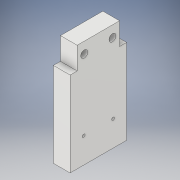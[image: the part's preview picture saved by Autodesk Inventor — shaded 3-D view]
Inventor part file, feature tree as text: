
AUTODESK INVENTOR PART (.ipt)
format: ipt  version: 2017 (Build 210142000, 142)  size: 136,192 bytes
history: native  units: in
note: dims shown in document units (in); Inventor stores cm internally (conversion verified against a paired STEP export)
features: extrude x2, sketch x2, projected_geometry x1
ambient origin geometry x8: Origin, YZ Plane, XZ Plane, XY Plane, X Axis, Y Axis, Z Axis, Center Point
bodies: Solid1 (feature_tree)
feature tree (5):
  extrude  "Extrusion1"  Depth=1.0in
  extrude  "Extrusion2"  Depth=0.2953in
  sketch  "Sketch1"  dims[d0=0.3937in d1=1.0in]
  sketch  "Sketch2"  dims[d2=0.25in d3=0.25in d4=0.125in d5=0.125in d6=0.75in d7=0.74in d8=0.7in d9=0.07in d10=0.09in d11=0.05in d12=0.2953in d13=0.0in d14=0.75in d15=0.2953in d16=0.0in]
  projected_geometry  "Projected Loop1"
